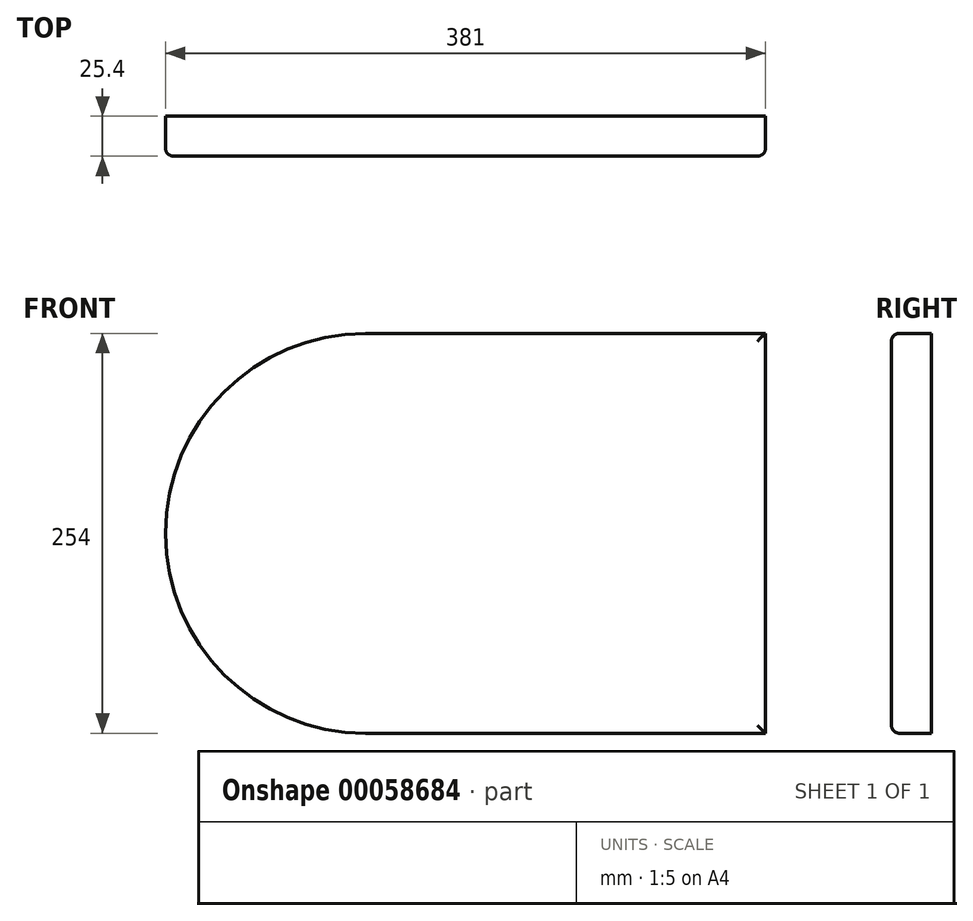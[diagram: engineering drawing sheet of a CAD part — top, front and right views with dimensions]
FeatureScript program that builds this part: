
annotation { "Feature Type Name" : "Feature", "Feature Type Description" : "" }
export const myFeature = defineFeature(function(context is Context, id is Id, definition is map)
    precondition{}
    {
        {
            var Q0;
            Q0=qCreatedBy(makeId("Front.planeOp"),FACE);
            var sketch = newSketch(context, id + "F0", { "sketchPlane" : qUnion([Q0])});
            skArc(sketch, "E0", {"start": v(0, 127) * mm, "mid": v(-127, 0) * mm, "end": v(0, -127) * mm});
            skLineSegment(sketch, "E1", {"start": v(0, 127) * mm, "end": v(0, -127) * mm});
            skSolve(sketch);
        }
        {
            var Q0;
            Q0=makeQuery(id+"F0.imprint","IMPRINT",FACE,{"disambiguationData":[TD([[makeQuery(id+"F0.imprint","IMPRINT",EDGE,{"derivedFrom":sQuery(id+"F0.wireOp",EDGE,"E0")}),1.0]])]});
            extrude(context, id + "F1", {"entities" : qUnion([Q0]), "endBound" : BoundingType.SYMMETRIC, "depth" : 25.4 * mm});
        }
        {
            var Q0;
            Q0=makeQuery(id+"F1.opExtrude","SWEPT_FACE",FACE,{"disambiguationData":[OSD([sQuery(id+"F0.wireOp",EDGE,"E1")])]});
            var sketch = newSketch(context, id + "F2", { "sketchPlane" : qUnion([Q0])});
            skLineSegment(sketch, "E2.rect.bottom", {"start": v(12.7, 127) * mm, "end": v(-12.7, 127) * mm});
            skLineSegment(sketch, "E2.rect.top", {"start": v(12.7, -127) * mm, "end": v(-12.7, -127) * mm});
            skLineSegment(sketch, "E2.rect.left", {"start": v(12.7, 127) * mm, "end": v(12.7, -127) * mm});
            skLineSegment(sketch, "E2.rect.right", {"start": v(-12.7, 127) * mm, "end": v(-12.7, -127) * mm});
            skPoint(sketch, "E2.rect.middle", {"position": v(0, 0) * mm});
            skSolve(sketch);
        }
        {
            var Q0;
            Q0 = qSketchRegion(id + "F2", true);
            extrude(context, id + "F3", {"entities" : qUnion([Q0]), "operationType" : NewBodyOperationType.ADD, "depth" : 254 * mm});
        }
        {
            var Q0;
            Q0=makeQuery(id+"F3.opExtrude","SWEPT_EDGE",EDGE,{"disambiguationData":[OSD([sQuery(id+"F2.wireOp",EDGE,"E2.rect.bottom"),sQuery(id+"F2.wireOp",EDGE,"E2.rect.right")])]});
            var Q1;
            Q1=makeQuery(id+"F3.opExtrude","CAP_EDGE",EDGE,{"disambiguationData":[OSD([sQuery(id+"F2.wireOp",EDGE,"E2.rect.right")])],"isStart":false});
            fillet(context, id + "F4", {"entities" : qUnion([Q0, Q1]), "radius" : 5.08 * mm, "tangentPropagation" : true, "allowEdgeOverflow" : false});
        }
    });
